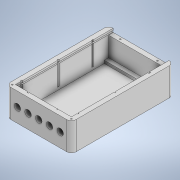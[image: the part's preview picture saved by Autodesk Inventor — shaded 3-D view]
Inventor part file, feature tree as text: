
AUTODESK INVENTOR PART (.ipt)
format: ipt  version: 2020 (Build 240168000, 168)  size: 561,152 bytes
history: native  units: mm
features: sketch x10, extrude x8, fillet x6, hole x3, plane x1
ambient origin geometry x8: Origin, YZ Plane, XZ Plane, XY Plane, X Axis, Y Axis, Z Axis, Center Point
bodies: Solid1 (feature_tree)
feature tree (28):
  sketch  "Sketch1"  dims[d0=60.0mm d1=100.0mm]
  extrude  "Extrusion1"  Depth=100.0mm
  extrude  "Extrusion2"  Depth=110.0mm
  fillet  "Fillet1"  Radius=30.0mm
  extrude  "Extrusion3"  Depth=5.0mm
  plane  "Work Plane1"
  extrude  "Extrusion4"  Depth=10.0mm TaperAngle=0.0deg
  extrude  "Extrusion5"  Depth=2.0mm
  hole  "Hole1"  [1 undecoded]
  hole  "Hole3"  [1 undecoded]
  hole  "Hole4"  [1 undecoded]
  extrude  "Extrusion6"  Depth=3.0mm
  fillet  "Fillet2"  Radius=7.0mm
  fillet  "Fillet3"  Radius=2.5mm
  extrude  "Extrusion7"  TaperAngle=45.0deg  [1 undecoded]
  fillet  "Fillet4"  Radius=2.5mm
  fillet  "Fillet5"  [1 undecoded]
  extrude  "Extrusion8"  Depth=20.0mm
  fillet  "Fillet6"  [1 undecoded]
  sketch  "Sketch2"  dims[d2=70.0mm d3=110.0mm d4=30.0mm d5=0.0mm]
  sketch  "Sketch3"  dims[d6=5.0mm d7=0.0mm d8=5.0mm]
  sketch  "Sketch4"  dims[d9=4.0mm d10=10.0mm d11=0.0mm]
  sketch  "Sketch5"  dims[d12=0.25mm d17=2.0mm]
  sketch  "Sketch7"  dims[d19=1.5mm d20=63.0mm]
  sketch  "Sketch8"  dims[d21=1.5mm d22=105.0mm d23=0.0mm]
  sketch  "Sketch9"  dims[d24=41.0mm d25=73.0mm]
  sketch  "Sketch10"  dims[d26=3.0mm d27=0.0mm d28=7.0mm d29=7.0mm]
  sketch  "Sketch11"  dims[d30=50.0mm d32=11.5mm d33=10.0mm d35=10.0mm d37=7.0mm d38=6.0mm d39=3.023mm d40=2.0mm d41=14.3117mm d42=8.0mm d43=20.594885mm d55=2.5mm d56=45.0deg d57=2.5mm d58=135.0deg d59=1.5mm d60=6.0mm d61=2.5mm d62=1.0mm d63=14.3117mm d64=40.0mm d65=20.594885mm d66=20.0mm d67=180.0deg d68=20.0mm d69=1.5mm d70=6.0mm d71=2.5mm d72=1.0mm d73=14.3117mm d74=40.0mm d75=20.594885mm d76=1.0mm d77=100.0mm d78=62.0mm d79=2.0mm d80=25.0mm d81=0.0mm d82=1.0mm d83=1.0mm d84=62.0mm d85=2.0mm d86=62.0mm d87=2.0mm d88=35.0mm d90=45.0mm d91=43.27457mm d92=25.0mm d93=0.0mm d94=1.0mm d95=1.0mm d96=1.0mm d97=2.0mm d98=2.0mm d100=13.0mm d101=13.0mm d102=2.0mm d103=1.0mm d104=25.0mm d105=0.0mm d106=1.0mm]
note: 6 required parameter values undecoded (feature->parameter linkage not recoverable at this tier; creation-order binding heuristic only, values carry confidence <= 0.55)
